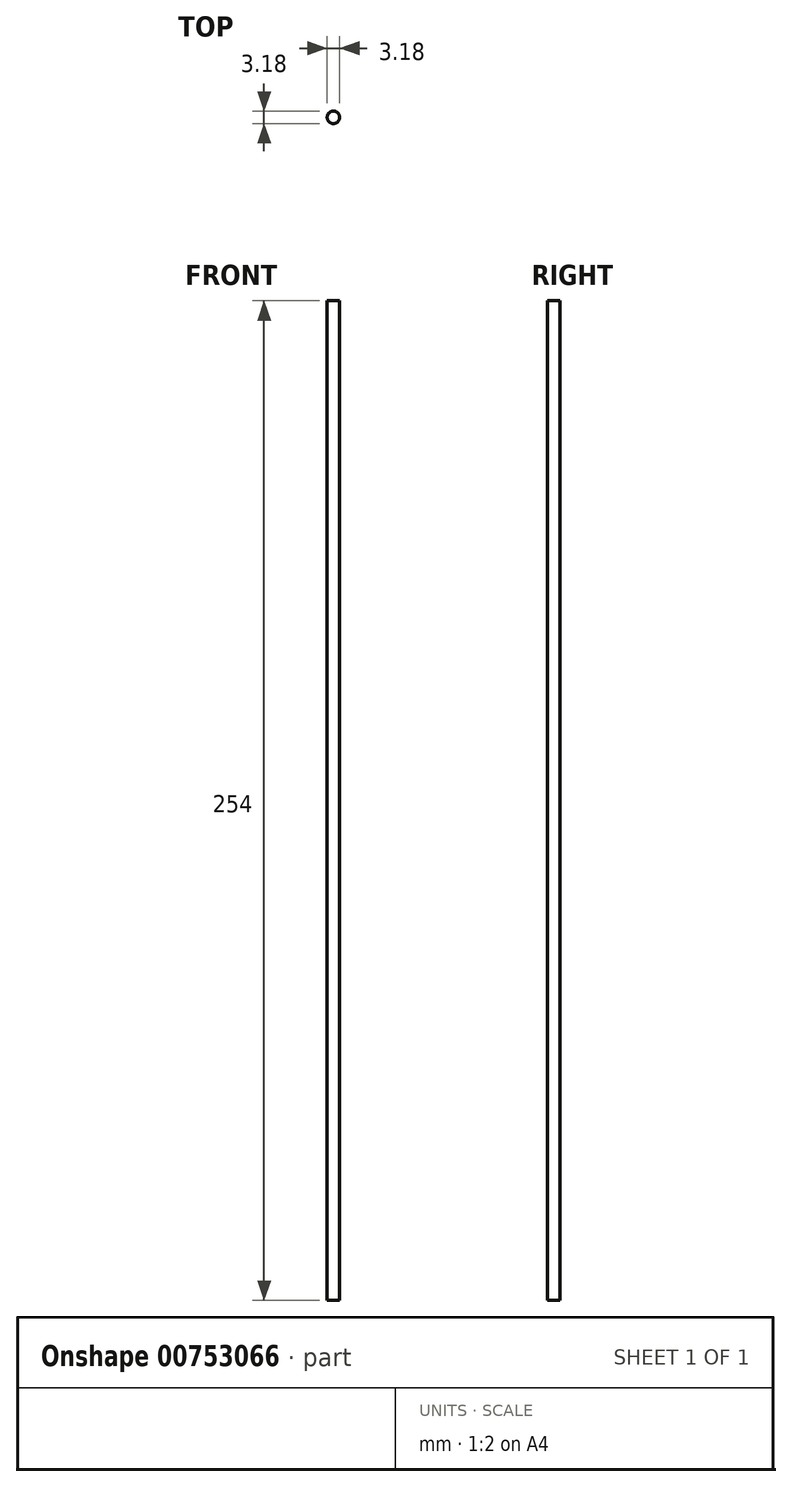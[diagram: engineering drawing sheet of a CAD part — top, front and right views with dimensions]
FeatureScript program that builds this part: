
annotation { "Feature Type Name" : "Feature", "Feature Type Description" : "" }
export const myFeature = defineFeature(function(context is Context, id is Id, definition is map)
    precondition{}
    {
        {
            var Q0;
            Q0=qCreatedBy(makeId("Top.planeOp"),FACE);
            var sketch = newSketch(context, id + "F0", { "sketchPlane" : qUnion([Q0])});
            skCircle(sketch, "E0", {"center": v(0, 0) * mm, "radius": 1.59 * mm});
            skSolve(sketch);
        }
        {
            var Q0;
            Q0=makeQuery(id+"F0.imprint","IMPRINT",FACE,{"disambiguationData":[TD([[makeQuery(id+"F0.imprint","IMPRINT",EDGE,{"derivedFrom":sQuery(id+"F0.wireOp",EDGE,"E0")}),1.0]])]});
            extrude(context, id + "F1", {"entities" : qUnion([Q0]), "depth" : 254 * mm, "offsetDistance" : 25.4 * mm});
        }
    });
